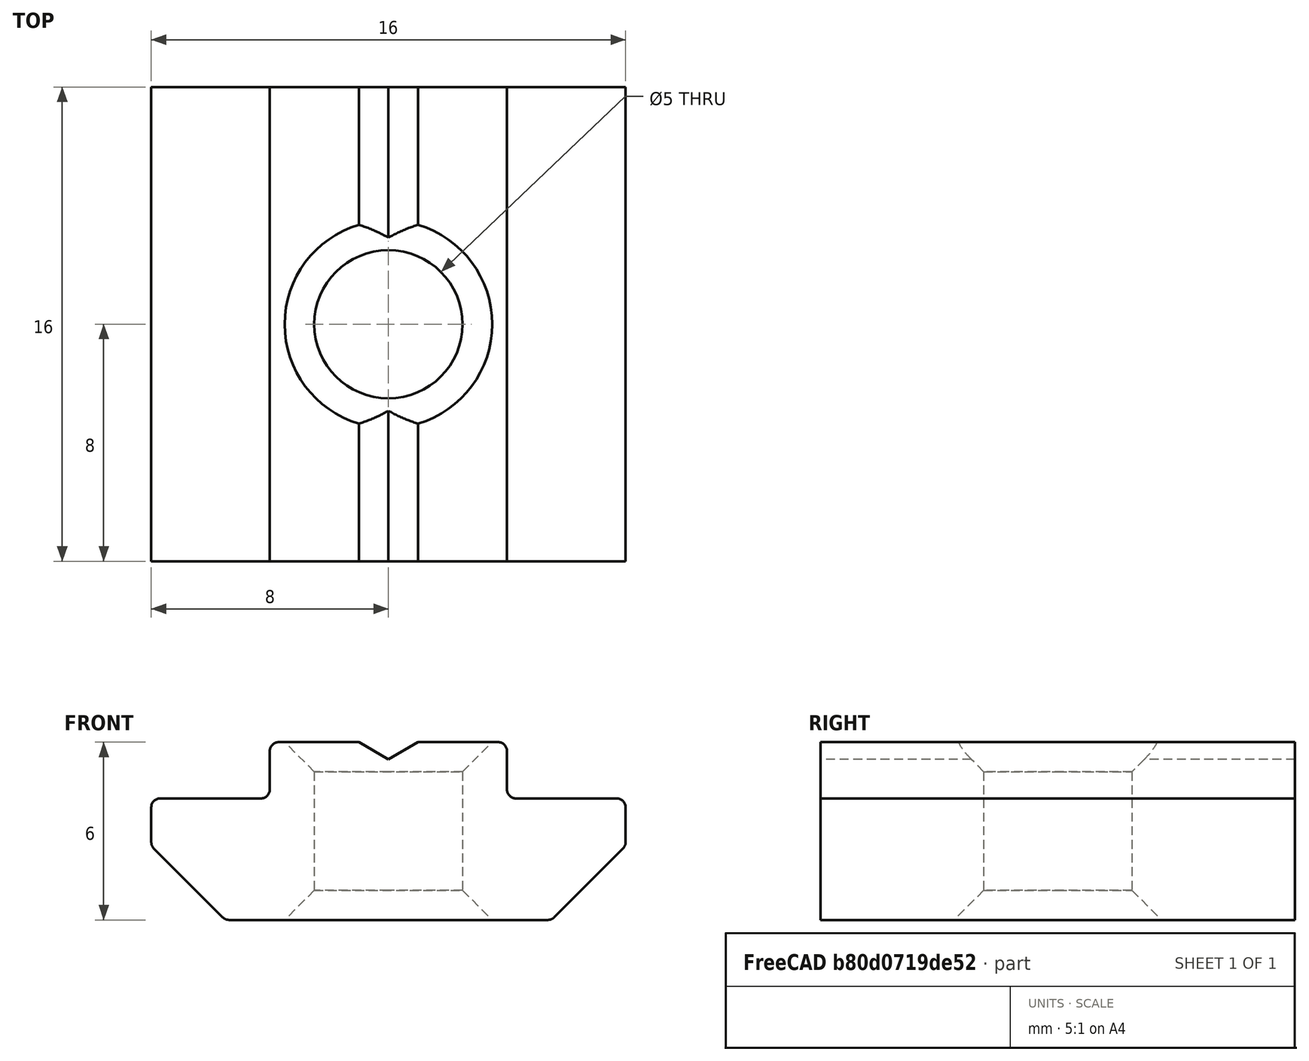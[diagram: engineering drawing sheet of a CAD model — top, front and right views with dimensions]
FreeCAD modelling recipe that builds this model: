
FCSTD DOCUMENT  (FreeCAD 0.19R20514 (Git))
Label: AP3030S8_StoneM6Heavy
Comment: FreeCAD-Library by episource -- https://github.com/episource/FreeCAD-Library
License: Creative Commons Attribution
LicenseURL: http://creativecommons.org/licenses/by/4.0/
objects: TechDraw::DrawViewDimension×10, Sketcher::SketchObject×3, TechDraw::DrawViewPart×2, TechDraw::DrawViewClip×2, TechDraw::DrawSVGTemplate×1, PartDesign::CoordinateSystem×1, App::DocumentObjectGroup×1, PartDesign::Pad×1, PartDesign::Hole×1, PartDesign::Groove×1, PartDesign::Body×1, TechDraw::DrawPage×1, App::Part×1
note: 11 computed .brp shape members not serialized (recipe doc carries the construction recipe); baked Part::Feature solids carry a one-line shape summary decoded from their .brp

FEATURE [Sketcher::SketchObject] Sketch001  label="PocketM6"
  Placement = pos=(0,0,6) rot=(0,0,1;0rad)
  sketch-geometry (1):
    g0: Circle CenterX=0 CenterY=0 CenterZ=0 NormalX=0 NormalY=0 NormalZ=1 AngleXU=0 Radius=0.715801
  constraints (1):
    c: Coincident(g0,g-1)
FEATURE [TechDraw::DrawSVGTemplate] Template
  EditableTexts = FC-SC=Scale 2:1 [mm]
  Height = 210
  Orientation = 1
  Width = 297
FEATURE [PartDesign::CoordinateSystem] AssyMount
  AttacherType = Attacher::AttachEngine3D
  AttachmentOffset = pos=(0,0,6.3) rot=(0,0,1;0rad)
  MapMode = 5
  Placement = pos=(0,0,6.3) rot=(0,0,1;0rad)
  Support = -> [XY_Plane]
  expr: .AttachmentOffset.Base.z = <<Variables>>.StoneHeight + <<Variables>>.ProfileSlotRise - <<Variables>>.StoneRise
FEATURE [App::DocumentObjectGroup] Group  label="Variables"
  ProfileSlotRise = 2.2
  ScrewHoleBevelSize = 1
  SlotWidth = 8
  StoneFillet = 0.3
  StoneHeight = 6
  StoneLength = 16
  StoneOuterRise = 1.6
  StoneTopNotchDepth = 0.58
  StoneTopNotchWidth = 2
  StoneTopRise = 1.9
  StoneWidth = 16
FEATURE [Sketcher::SketchObject] Sketch  label="StoneSectionSketch"
  MapMode = 5
  Placement = pos=(0,0,0) rot=(1,0,0;1.5708rad)
  Support = -> [XZ_Plane]
  expr: Constraints[64] = <<Variables>>.StoneOuterRise
  expr: Constraints[11] = <<Variables>>.SlotWidth
  expr: Constraints[12] = <<Variables>>.StoneWidth
  expr: Constraints[13] = <<Variables>>.StoneHeight
  expr: Constraints[25] = <<Variables>>.StoneTopNotchDepth
  expr: Constraints[21] = <<Variables>>.StoneFillet
  expr: Constraints[27] = <<Variables>>.StoneTopNotchWidth
  expr: Constraints[17] = <<Variables>>.StoneFillet
  expr: Constraints[14] = <<Variables>>.StoneTopRise
  expr: Constraints[22] = <<Variables>>.StoneFillet
  expr: Constraints[24] = <<Variables>>.StoneFillet
  expr: Constraints[20] = <<Variables>>.StoneFillet
  expr: Constraints[15] = <<Variables>>.StoneFillet
  expr: Constraints[18] = <<Variables>>.StoneFillet
  expr: Constraints[19] = <<Variables>>.StoneFillet
  expr: Constraints[23] = <<Variables>>.StoneFillet
  expr: Constraints[16] = <<Variables>>.StoneFillet
  sketch-geometry (26):
    g0: LineSegment StartX=-1 StartY=6 StartZ=0 EndX=-3.7 EndY=6 EndZ=0
    g1: ArcOfCircle CenterX=-3.7 CenterY=5.7 CenterZ=0 NormalX=0 NormalY=0 NormalZ=1 AngleXU=3.14159 Radius=0.3 StartAngle=4.71239 EndAngle=6.28319
    g2: LineSegment StartX=-4 StartY=5.7 StartZ=0 EndX=-4 EndY=4.4 EndZ=0
    g3: ArcOfCircle CenterX=-4.3 CenterY=4.4 CenterZ=0 NormalX=0 NormalY=0 NormalZ=1 AngleXU=-3.14159 Radius=0.3 StartAngle=1.5708 EndAngle=3.14159
    g4: LineSegment StartX=-4.3 StartY=4.1 StartZ=0 EndX=-7.7 EndY=4.1 EndZ=0
    g5: ArcOfCircle CenterX=-7.7 CenterY=3.8 CenterZ=0 NormalX=0 NormalY=0 NormalZ=1 AngleXU=-3.14159 Radius=0.3 StartAngle=4.71239 EndAngle=6.28319
    g6: LineSegment StartX=-8 StartY=3.8 StartZ=0 EndX=-8 EndY=2.62426 EndZ=0
    g7: ArcOfCircle CenterX=-7.7 CenterY=2.62426 CenterZ=0 NormalX=0 NormalY=0 NormalZ=1 AngleXU=-3.14159 Radius=0.3 StartAngle=0 EndAngle=0.785398
    g8: LineSegment StartX=-7.91213 StartY=2.41213 StartZ=0 EndX=-5.58787 EndY=0.087868 EndZ=0
    g9: ArcOfCircle CenterX=-5.37574 CenterY=0.3 CenterZ=0 NormalX=0 NormalY=0 NormalZ=1 AngleXU=3.14159 Radius=0.3 StartAngle=0.785398 EndAngle=1.5708
    g10: LineSegment StartX=-5.37574 StartY=0 StartZ=0 EndX=5.37574 EndY=0 EndZ=0
    g11: ArcOfCircle CenterX=5.37574 CenterY=0.3 CenterZ=0 NormalX=0 NormalY=0 NormalZ=1 AngleXU=-3.14159 Radius=0.3 StartAngle=1.5708 EndAngle=2.35619
    g12: LineSegment StartX=5.58787 StartY=0.087868 StartZ=0 EndX=7.91213 EndY=2.41213 EndZ=0
    g13: ArcOfCircle CenterX=7.7 CenterY=2.62426 CenterZ=0 NormalX=0 NormalY=0 NormalZ=1 AngleXU=-3.14159 Radius=0.3 StartAngle=2.35619 EndAngle=3.14159
    g14: LineSegment StartX=8 StartY=2.62426 StartZ=0 EndX=8 EndY=3.8 EndZ=0
    g15: ArcOfCircle CenterX=7.7 CenterY=3.8 CenterZ=0 NormalX=0 NormalY=0 NormalZ=1 AngleXU=-3.14159 Radius=0.3 StartAngle=3.14159 EndAngle=4.71239
    g16: LineSegment StartX=7.7 StartY=4.1 StartZ=0 EndX=4.3 EndY=4.1 EndZ=0
    g17: ArcOfCircle CenterX=4.3 CenterY=4.4 CenterZ=0 NormalX=0 NormalY=0 NormalZ=1 AngleXU=-3.14159 Radius=0.3 StartAngle=0 EndAngle=1.5708
    g18: LineSegment StartX=4 StartY=4.4 StartZ=0 EndX=4 EndY=5.7 EndZ=0
    g19: ArcOfCircle CenterX=3.7 CenterY=5.7 CenterZ=0 NormalX=0 NormalY=0 NormalZ=1 AngleXU=-3.14159 Radius=0.3 StartAngle=3.14159 EndAngle=4.71239
    g20: LineSegment StartX=3.7 StartY=6 StartZ=0 EndX=1 EndY=6 EndZ=0
    g21: LineSegment StartX=1 StartY=6 StartZ=0 EndX=0 EndY=5.42 EndZ=0
    g22: LineSegment StartX=0 StartY=5.42 StartZ=0 EndX=-1 EndY=6 EndZ=0
    g23: LineSegment [constr] StartX=4.3 StartY=4.1 StartZ=0 EndX=8 EndY=4.1 EndZ=0
    g24: LineSegment [constr] StartX=8 StartY=4.1 StartZ=0 EndX=8 EndY=2.5 EndZ=0
    g25: LineSegment [constr] StartX=5.58787 StartY=0.087868 StartZ=0 EndX=8 EndY=2.5 EndZ=0
  constraints (65):
    c: Horizontal(g4)
    c: Vertical(g6)
    c: Vertical(g14)
    c: Coincident(g20,g21)
    c: Coincident(g21,g22)
    c: Coincident(g22,g0)
    c: Vertical(g2)
    c: Vertical(g18)
    c: Horizontal(g10)
    c: Horizontal(g0)
    c: Horizontal(g20)
    c: DistanceX(g1,g18) = 8
    c: DistanceX(g5,g14) = 16
    c: DistanceY(g9,g0) = 6
    c: DistanceY(g16,g19) = 1.9
    c: Radius(g17) = 0.3
    c: Radius(g3) = 0.3
    c: Radius(g5) = 0.3
    c: Radius(g15) = 0.3
    c: Radius(g1) = 0.3
    c: Radius(g19) = 0.3
    c: Radius(g13) = 0.3
    c: Radius(g7) = 0.3
    c: Radius(g11) = 0.3
    c: Radius(g9) = 0.3
    c: DistanceY(g21,g20) = 0.58
    c: PointOnObject(g21,g-2)
    c: DistanceX(g0,g20) = 2
    c: Equal(g0,g20)
    c: Equal(g2,g18)
    c: Equal(g4,g16)
    c: Equal(g12,g8)
    c: Symmetric(g9,g10,g-1)
    c: Angle(g8,g6) = 2.35619
    c: Angle(g14,g12) = 2.35619
    c: Symmetric(g0,g20,g-2)
    c: Tangent(g0,g1) = -1.5708
    c: Tangent(g1,g2) = -1.5708
    c: Tangent(g19,g20) = -1.5708
    c: Tangent(g18,g19) = -1.5708
    c: Tangent(g17,g18) = 1.5708
    c: Tangent(g16,g17) = 1.5708
    c: Tangent(g15,g16) = -1.5708
    c: Tangent(g14,g15) = -1.5708
    c: Tangent(g13,g14) = -1.5708
    c: Tangent(g12,g13) = -1.5708
    c: Tangent(g11,g12) = -1.5708
    c: Tangent(g10,g11) = -1.5708
    c: Tangent(g9,g10) = -1.5708
    c: Tangent(g8,g9) = -1.5708
    c: Tangent(g7,g8) = -1.5708
    c: Tangent(g6,g7) = -1.5708
    c: Tangent(g5,g6) = -1.5708
    c: Tangent(g4,g5) = -1.5708
    c: Tangent(g3,g4) = 1.5708
    c: Tangent(g2,g3) = 1.5708
    c: Coincident(g23,g16)
    c: PointOnObject(g15,g23)
    c: PointOnObject(g13,g24)
    c: PointOnObject(g14,g24)
    c: PointOnObject(g12,g25)
    c: Coincident(g24,g23)
    c: Coincident(g25,g11)
    c: Coincident(g24,g25)
    c: DistanceY(g24,g23) = 1.6
FEATURE [PartDesign::Pad] Pad
  AllowMultiFace = false
  Length = 16
  Length2 = 100
  Midplane = true
  Placement = pos=(0,0,0) rot=(1,0,0;1.5708rad)
  Profile = -> Sketch
  Type = 0
FEATURE [PartDesign::Hole] Hole
  AllowMultiFace = false
  BaseFeature = -> Pad
  Depth = 25
  DepthType = 1
  Diameter = 5
  DrillPoint = 1
  DrillPointAngle = 118
  HoleCutCountersinkAngle = 90
  HoleCutDepth = 0
  HoleCutDiameter = 6
  HoleCutType = 0
  ModelActualThread = false
  Placement = pos=(0,0,0) rot=(1,0,0;1.5708rad)
  Profile = -> Sketch001
  Tapered = false
  TaperedAngle = 90
  ThreadAngle = 60
  ThreadClass = 0
  ThreadCutOffInner = 0.108253
  ThreadCutOffOuter = 0.216506
  ThreadDirection = 0
  ThreadFit = 0
  ThreadPitch = 1
  ThreadSize = 7
  ThreadType = 1
  Threaded = true
FEATURE [Sketcher::SketchObject] Sketch002  label="SketchScrewHoleBevel"
  ExternalGeometry = -> [Hole]
  MapMode = 5
  Placement = pos=(0,0,0) rot=(0.57735,0.57735,0.57735;2.0944rad)
  Support = -> [YZ_Plane]
  expr: Constraints[5] = <<Variables>>.ScrewHoleBevelSize
  expr: Constraints[6] = <<Variables>>.StoneHeight
  sketch-geometry (8):
    g0: LineSegment [constr] StartX=2.5 StartY=0 StartZ=0 EndX=2.5 EndY=6 EndZ=0
    g1: LineSegment [constr] StartX=3.5 StartY=0 StartZ=0 EndX=3.5 EndY=6 EndZ=0
    g2: LineSegment StartX=2.5 StartY=6 StartZ=0 EndX=3.5 EndY=6 EndZ=0
    g3: LineSegment StartX=3.5 StartY=6 StartZ=0 EndX=2.5 EndY=5 EndZ=0
    g4: LineSegment StartX=2.5 StartY=5 StartZ=0 EndX=2.5 EndY=6 EndZ=0
    g5: LineSegment StartX=2.5 StartY=0 StartZ=0 EndX=2.5 EndY=1 EndZ=0
    g6: LineSegment StartX=2.5 StartY=1 StartZ=0 EndX=3.5 EndY=0 EndZ=0
    g7: LineSegment StartX=3.5 StartY=0 StartZ=0 EndX=2.5 EndY=0 EndZ=0
  constraints (22):
    c: PointOnObject(g0,g-1)
    c: Vertical(g0)
    c: PointOnObject(g-3,g0)
    c: Vertical(g1)
    c: PointOnObject(g1,g-1)
    c: DistanceX(g0,g1) = 1
    c: DistanceY(g0,g0) = 6
    c: Equal(g0,g1)
    c: Coincident(g0,g2)
    c: Coincident(g2,g1)
    c: Coincident(g2,g3)
    c: PointOnObject(g3,g0)
    c: Coincident(g3,g4)
    c: Coincident(g4,g2)
    c: Equal(g4,g2)
    c: Coincident(g0,g5)
    c: PointOnObject(g5,g0)
    c: Coincident(g5,g6)
    c: Coincident(g6,g1)
    c: Coincident(g6,g7)
    c: Coincident(g7,g5)
    c: Equal(g5,g7)
FEATURE [PartDesign::Groove] Groove  label="ScrewHoleBevel"
  Angle = 360
  Axis = (-2e-16,3e-16,1)
  Base = (0,0,0)
  BaseFeature = -> Hole
  Placement = pos=(0,0,0) rot=(1,0,0;1.5708rad)
  Profile = -> Sketch002
  ReferenceAxis = -> Sketch002 [V_Axis]
FEATURE [PartDesign::Body] Body
  Group = -> [Pad,Sketch001,Hole,Sketch,Sketch002,Groove]
  Origin = -> Origin
  Tip = -> Groove
FEATURE [TechDraw::DrawViewPart] View
  CoarseView = false
  Direction = (0,0,1)
  Focus = 100
  HardHidden = false
  IsoCount = 0
  IsoHidden = false
  IsoVisible = false
  LockPosition = false
  Perspective = false
  Rotation = 0
  Scale = 2
  ScaleType = 0
  SeamHidden = false
  SeamVisible = false
  SmoothHidden = false
  SmoothVisible = false
  Source = -> [Body]
  X = 0
  XDirection = (1,0,0)
  Y = -3
FEATURE [TechDraw::DrawViewClip] Clip  label="Top View"
  Height = 60
  LockPosition = false
  Rotation = 0
  Scale = 2
  ScaleType = 0
  ShowFrame = false
  Views = -> [View]
  Width = 100
  X = 75
  Y = 110
FEATURE [TechDraw::DrawViewDimension] Dimension003
  Arbitrary = false
  FormatSpec = %.1f
  Inverted = false
  LockPosition = false
  MeasureType = 1
  OverTolerance = 0
  References2D = -> [View]
  Rotation = 0
  Scale = 2
  ScaleType = 0
  TheoreticalExact = false
  Type = 2
  UnderTolerance = 0
  X = -26.0269
  Y = 0.752239
FEATURE [TechDraw::DrawViewPart] View001
  CoarseView = false
  Direction = (0,-1,0)
  Focus = 100
  HardHidden = false
  IsoCount = 0
  IsoHidden = false
  IsoVisible = false
  LockPosition = false
  Perspective = false
  Rotation = 0
  Scale = 2
  ScaleType = 0
  SeamHidden = false
  SeamVisible = false
  SmoothHidden = false
  SmoothVisible = false
  Source = -> [Body]
  X = 0
  XDirection = (1,0,0)
  Y = 0
FEATURE [TechDraw::DrawViewClip] Clip001  label="Front View"
  Height = 50
  LockPosition = false
  Rotation = 0
  Scale = 2
  ScaleType = 0
  ShowFrame = false
  Views = -> [View001]
  Width = 100
  X = 222
  Y = 110
FEATURE [TechDraw::DrawViewDimension] Dimension004
  Arbitrary = false
  FormatSpec = %.1f
  Inverted = false
  LockPosition = false
  MeasureType = 1
  OverTolerance = 0
  References2D = -> [View001]
  Rotation = 0
  Scale = 2
  ScaleType = 0
  TheoreticalExact = false
  Type = 2
  UnderTolerance = 0
  X = -30.0026
  Y = -1.62532
FEATURE [TechDraw::DrawViewDimension] Dimension005
  Arbitrary = false
  FormatSpec = %.1f
  Inverted = false
  LockPosition = false
  MeasureType = 1
  OverTolerance = 0
  References2D = -> [View001]
  Rotation = 0
  Scale = 2
  ScaleType = 0
  TheoreticalExact = false
  Type = 2
  UnderTolerance = 0
  X = 21.6395
  Y = 0.824036
FEATURE [TechDraw::DrawViewDimension] Dimension006
  Arbitrary = false
  FormatSpec = %.1f
  Inverted = false
  LockPosition = false
  MeasureType = 1
  OverTolerance = 0
  References2D = -> [View001]
  Rotation = 0
  Scale = 2
  ScaleType = 0
  TheoreticalExact = false
  Type = 1
  UnderTolerance = 0
  X = -0.572247
  Y = -10.8941
FEATURE [TechDraw::DrawViewDimension] Dimension007
  Arbitrary = false
  FormatSpec = %.1f
  Inverted = false
  LockPosition = false
  MeasureType = 1
  OverTolerance = 0
  References2D = -> [View001]
  Rotation = 0
  Scale = 2
  ScaleType = 0
  TheoreticalExact = false
  Type = 1
  UnderTolerance = 0
  X = 13.3352
  Y = 13.4542
FEATURE [TechDraw::DrawViewDimension] Dimension008
  Arbitrary = false
  FormatSpec = %.1f
  Inverted = false
  LockPosition = false
  MeasureType = 1
  OverTolerance = 0
  References2D = -> [View001]
  Rotation = 0
  Scale = 2
  ScaleType = 0
  TheoreticalExact = false
  Type = 1
  UnderTolerance = 0
  X = 0.476873
  Y = 20.1582
FEATURE [TechDraw::DrawViewDimension] Dimension009
  Arbitrary = false
  FormatSpec = %.1f
  Inverted = false
  LockPosition = false
  MeasureType = 1
  OverTolerance = 0
  References2D = -> [View001]
  Rotation = 0
  Scale = 2
  ScaleType = 0
  TheoreticalExact = false
  Type = 2
  UnderTolerance = 0
  X = -21.6866
  Y = 7.86119
FEATURE [TechDraw::DrawViewDimension] Dimension
  Arbitrary = false
  FormatSpec = %.1f
  Inverted = false
  LockPosition = false
  MeasureType = 1
  OverTolerance = 0
  References2D = -> [View]
  Rotation = 0
  Scale = 2
  ScaleType = 0
  TheoreticalExact = false
  Type = 1
  UnderTolerance = 0
  X = 0.276739
  Y = 22.4196
FEATURE [TechDraw::DrawViewDimension] Dimension010
  Arbitrary = false
  FormatSpec = %.1f
  Inverted = false
  LockPosition = false
  MeasureType = 1
  OverTolerance = 0
  References2D = -> [View]
  Rotation = 0
  Scale = 2
  ScaleType = 0
  TheoreticalExact = false
  Type = 1
  UnderTolerance = 0
  X = 12.1468
  Y = 29.2987
FEATURE [TechDraw::DrawViewDimension] Dimension011
  Arbitrary = false
  FormatSpec = %.1f
  Inverted = false
  LockPosition = false
  MeasureType = 1
  OverTolerance = 0
  References2D = -> [View]
  Rotation = 0
  Scale = 2
  ScaleType = 0
  TheoreticalExact = false
  Type = 1
  UnderTolerance = 0
  X = -11.8138
  Y = 29.3106
FEATURE [TechDraw::DrawPage] Page  label="Spec"
  KeepUpdated = true
  NextBalloonIndex = 1
  ProjectionType = 0
  Scale = 2
  Template = -> Template
  Views = -> [View,Clip,Dimension003,Clip001,View001,Dimension004,Dimension005,Dimension006,Dimension007,Dimension008,Dimension009,Dimension,Dimension010,Dimension011]
FEATURE [App::Part] Part  label="AP3030S8_StoneM6Heavy"
  Group = -> [Body,Page,AssyMount,Group]
  Origin = -> Origin001
